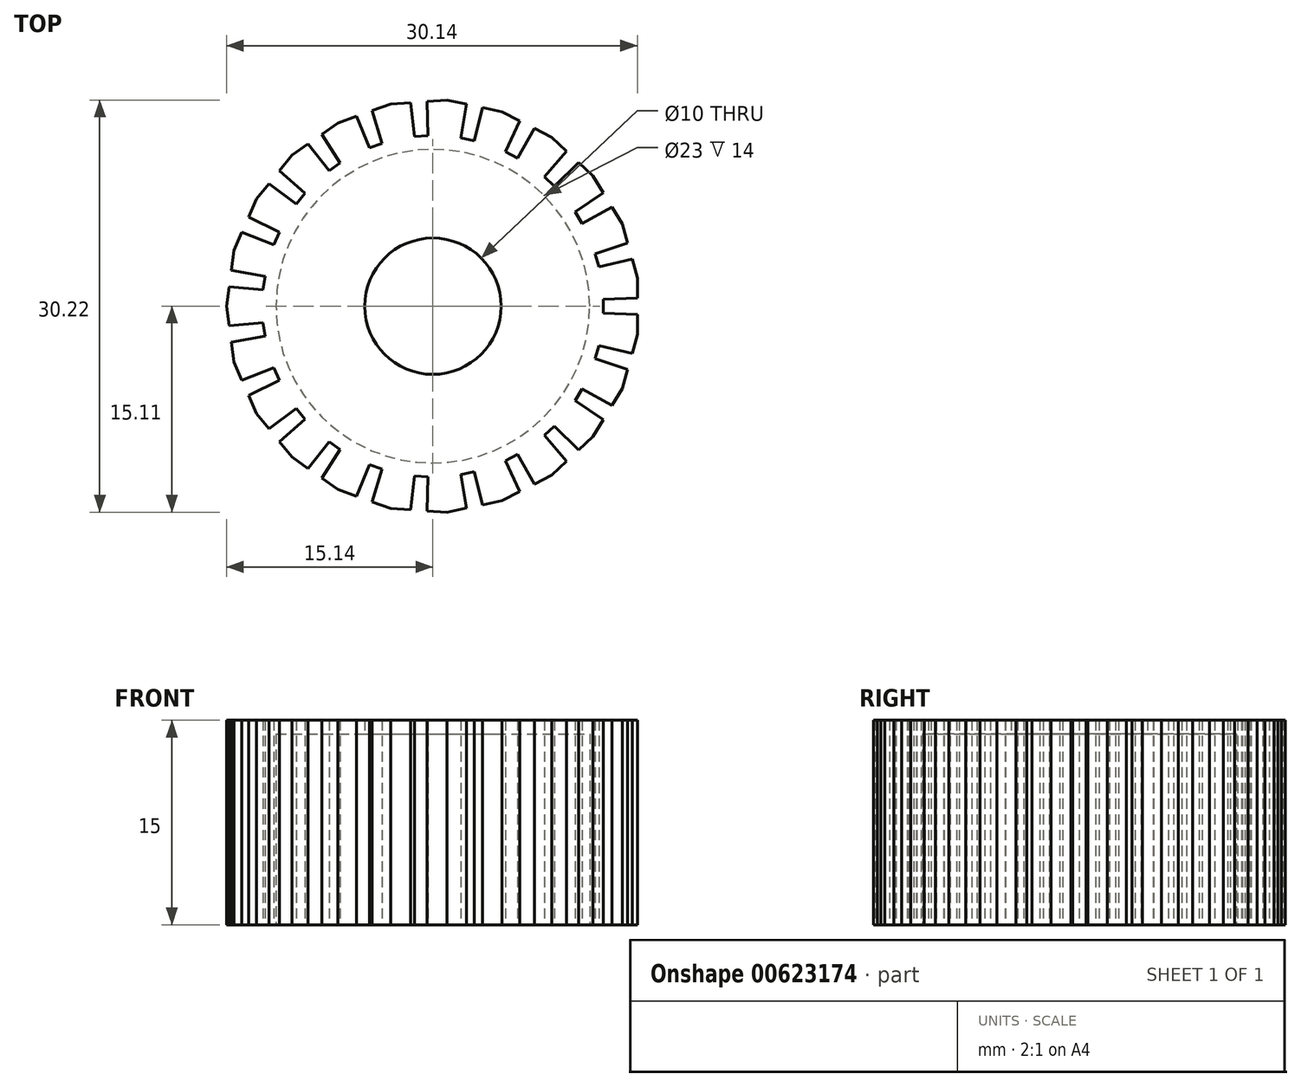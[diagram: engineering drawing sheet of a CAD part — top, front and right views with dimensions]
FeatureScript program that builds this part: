
annotation { "Feature Type Name" : "Feature", "Feature Type Description" : "" }
export const myFeature = defineFeature(function(context is Context, id is Id, definition is map)
    precondition{}
    {
        {
            var Q0;
            Q0=qCreatedBy(makeId("Top.planeOp"),FACE);
            var sketch = newSketch(context, id + "F0", { "sketchPlane" : qUnion([Q0])});
            skCircle(sketch, "E0", {"center": v(0, 0) * mm, "radius": 5 * mm});
            skCircle(sketch, "E1.cCircle", {"center": v(0, 0) * mm, "radius": 15 * mm, "construction": true});
            skLineSegment(sketch, "E1.0", {"start": v(15, 2.06) * mm, "end": v(15, 0.6) * mm});
            skLineSegment(sketch, "E1.1", {"start": v(15, -2.06) * mm, "end": v(13.89, -6.03) * mm, "construction": true});
            skLineSegment(sketch, "E1.2", {"start": v(13.89, -6.03) * mm, "end": v(11.75, -9.56) * mm, "construction": true});
            skLineSegment(sketch, "E1.3", {"start": v(11.75, -9.56) * mm, "end": v(8.73, -12.37) * mm, "construction": true});
            skLineSegment(sketch, "E1.4", {"start": v(8.73, -12.37) * mm, "end": v(5.07, -14.27) * mm, "construction": true});
            skLineSegment(sketch, "E1.5", {"start": v(5.07, -14.27) * mm, "end": v(1.03, -15.1) * mm, "construction": true});
            skLineSegment(sketch, "E1.6", {"start": v(1.03, -15.1) * mm, "end": v(-3.08, -14.82) * mm, "construction": true});
            skLineSegment(sketch, "E1.7", {"start": v(-3.08, -14.82) * mm, "end": v(-6.97, -13.44) * mm, "construction": true});
            skLineSegment(sketch, "E1.8", {"start": v(-6.97, -13.44) * mm, "end": v(-10.33, -11.07) * mm, "construction": true});
            skLineSegment(sketch, "E1.9", {"start": v(-10.33, -11.07) * mm, "end": v(-12.94, -7.87) * mm, "construction": true});
            skLineSegment(sketch, "E1.10", {"start": v(-12.94, -7.87) * mm, "end": v(-14.58, -4.08) * mm, "construction": true});
            skLineSegment(sketch, "E1.11", {"start": v(-14.58, -4.08) * mm, "end": v(-15.14, 0) * mm, "construction": true});
            skLineSegment(sketch, "E1.12", {"start": v(-15.14, 0) * mm, "end": v(-14.58, 4.08) * mm, "construction": true});
            skLineSegment(sketch, "E1.13", {"start": v(-14.58, 4.08) * mm, "end": v(-12.94, 7.87) * mm, "construction": true});
            skLineSegment(sketch, "E1.14", {"start": v(-12.94, 7.87) * mm, "end": v(-10.33, 11.07) * mm, "construction": true});
            skLineSegment(sketch, "E1.15", {"start": v(-10.33, 11.07) * mm, "end": v(-6.97, 13.44) * mm, "construction": true});
            skLineSegment(sketch, "E1.16", {"start": v(-6.97, 13.44) * mm, "end": v(-3.08, 14.82) * mm, "construction": true});
            skLineSegment(sketch, "E1.17", {"start": v(-3.08, 14.82) * mm, "end": v(1.03, 15.1) * mm, "construction": true});
            skLineSegment(sketch, "E1.18", {"start": v(1.03, 15.1) * mm, "end": v(5.07, 14.27) * mm, "construction": true});
            skLineSegment(sketch, "E1.19", {"start": v(5.07, 14.27) * mm, "end": v(8.73, 12.37) * mm, "construction": true});
            skLineSegment(sketch, "E1.20", {"start": v(8.73, 12.37) * mm, "end": v(11.75, 9.56) * mm, "construction": true});
            skLineSegment(sketch, "E1.21", {"start": v(11.75, 9.56) * mm, "end": v(13.89, 6.03) * mm, "construction": true});
            skLineSegment(sketch, "E1.22", {"start": v(13.89, 6.03) * mm, "end": v(15, 2.06) * mm, "construction": true});
            skPoint(sketch, "E1.0.midPoint", {"position": v(15, 0) * mm});
            skLineSegment(sketch, "E2", {"start": v(15, 0.6) * mm, "end": v(12.5, 0.5) * mm});
            skLineSegment(sketch, "E3", {"start": v(12.5, 0.5) * mm, "end": v(12.5, -0.5) * mm});
            skLineSegment(sketch, "E4", {"start": v(12.5, -0.5) * mm, "end": v(15, -0.6) * mm});
            skLineSegment(sketch, "E5.trimOffspring", {"start": v(15, -0.6) * mm, "end": v(15, -2.06) * mm});
            skLineSegment(sketch, "E6.1.0", {"start": v(13.89, 6.03) * mm, "end": v(14.28, 4.63) * mm});
            skLineSegment(sketch, "E6.1.1", {"start": v(14.28, 4.63) * mm, "end": v(11.9, 3.85) * mm});
            skLineSegment(sketch, "E6.1.2", {"start": v(12.17, 2.9) * mm, "end": v(14.6, 3.46) * mm});
            skLineSegment(sketch, "E6.1.3", {"start": v(11.9, 3.85) * mm, "end": v(12.17, 2.9) * mm});
            skLineSegment(sketch, "E6.1.4", {"start": v(14.6, 3.46) * mm, "end": v(15, 2.06) * mm});
            skLineSegment(sketch, "E6.2.0", {"start": v(11.75, 9.56) * mm, "end": v(12.5, 8.31) * mm});
            skLineSegment(sketch, "E6.2.1", {"start": v(12.5, 8.31) * mm, "end": v(10.42, 6.92) * mm});
            skLineSegment(sketch, "E6.2.2", {"start": v(10.94, 6.07) * mm, "end": v(13.13, 7.27) * mm});
            skLineSegment(sketch, "E6.2.3", {"start": v(10.42, 6.92) * mm, "end": v(10.94, 6.07) * mm});
            skLineSegment(sketch, "E6.2.4", {"start": v(13.13, 7.27) * mm, "end": v(13.89, 6.03) * mm});
            skLineSegment(sketch, "E6.3.0", {"start": v(8.73, 12.37) * mm, "end": v(9.8, 11.38) * mm});
            skLineSegment(sketch, "E6.3.1", {"start": v(9.8, 11.38) * mm, "end": v(8.17, 9.48) * mm});
            skLineSegment(sketch, "E6.3.2", {"start": v(8.9, 8.8) * mm, "end": v(10.68, 10.55) * mm});
            skLineSegment(sketch, "E6.3.3", {"start": v(8.17, 9.48) * mm, "end": v(8.9, 8.8) * mm});
            skLineSegment(sketch, "E6.3.4", {"start": v(10.68, 10.55) * mm, "end": v(11.75, 9.56) * mm});
            skLineSegment(sketch, "E6.4.0", {"start": v(5.07, 14.27) * mm, "end": v(6.36, 13.6) * mm});
            skLineSegment(sketch, "E6.4.1", {"start": v(6.36, 13.6) * mm, "end": v(5.3, 11.33) * mm});
            skLineSegment(sketch, "E6.4.2", {"start": v(6.2, 10.87) * mm, "end": v(7.44, 13.04) * mm});
            skLineSegment(sketch, "E6.4.3", {"start": v(5.3, 11.33) * mm, "end": v(6.2, 10.87) * mm});
            skLineSegment(sketch, "E6.4.4", {"start": v(7.44, 13.04) * mm, "end": v(8.73, 12.37) * mm});
            skLineSegment(sketch, "E6.5.0", {"start": v(1.03, 15.1) * mm, "end": v(2.46, 14.81) * mm});
            skLineSegment(sketch, "E6.5.1", {"start": v(2.46, 14.81) * mm, "end": v(2.05, 12.34) * mm});
            skLineSegment(sketch, "E6.5.2", {"start": v(3.03, 12.14) * mm, "end": v(3.65, 14.56) * mm});
            skLineSegment(sketch, "E6.5.3", {"start": v(2.05, 12.34) * mm, "end": v(3.03, 12.14) * mm});
            skLineSegment(sketch, "E6.5.4", {"start": v(3.65, 14.56) * mm, "end": v(5.07, 14.27) * mm});
            skLineSegment(sketch, "E6.6.0", {"start": v(-3.08, 14.82) * mm, "end": v(-1.63, 14.92) * mm});
            skLineSegment(sketch, "E6.6.1", {"start": v(-1.63, 14.92) * mm, "end": v(-1.35, 12.44) * mm});
            skLineSegment(sketch, "E6.6.2", {"start": v(-0.35, 12.5) * mm, "end": v(-0.42, 15) * mm});
            skLineSegment(sketch, "E6.6.3", {"start": v(-1.35, 12.44) * mm, "end": v(-0.35, 12.5) * mm});
            skLineSegment(sketch, "E6.6.4", {"start": v(-0.42, 15) * mm, "end": v(1.03, 15.1) * mm});
            skLineSegment(sketch, "E6.7.0", {"start": v(-6.97, 13.44) * mm, "end": v(-5.6, 13.93) * mm});
            skLineSegment(sketch, "E6.7.1", {"start": v(-5.6, 13.93) * mm, "end": v(-4.66, 11.61) * mm});
            skLineSegment(sketch, "E6.7.2", {"start": v(-3.71, 11.95) * mm, "end": v(-4.45, 14.34) * mm});
            skLineSegment(sketch, "E6.7.3", {"start": v(-4.66, 11.61) * mm, "end": v(-3.71, 11.95) * mm});
            skLineSegment(sketch, "E6.7.4", {"start": v(-4.45, 14.34) * mm, "end": v(-3.08, 14.82) * mm});
            skLineSegment(sketch, "E6.8.0", {"start": v(-10.33, 11.07) * mm, "end": v(-9.15, 11.9) * mm});
            skLineSegment(sketch, "E6.8.1", {"start": v(-9.15, 11.9) * mm, "end": v(-7.62, 9.92) * mm});
            skLineSegment(sketch, "E6.8.2", {"start": v(-6.8, 10.5) * mm, "end": v(-8.15, 12.6) * mm});
            skLineSegment(sketch, "E6.8.3", {"start": v(-7.62, 9.92) * mm, "end": v(-6.8, 10.5) * mm});
            skLineSegment(sketch, "E6.8.4", {"start": v(-8.15, 12.6) * mm, "end": v(-6.97, 13.44) * mm});
            skLineSegment(sketch, "E6.9.0", {"start": v(-12.94, 7.87) * mm, "end": v(-12.02, 9) * mm});
            skLineSegment(sketch, "E6.9.1", {"start": v(-12.02, 9) * mm, "end": v(-10.01, 7.5) * mm});
            skLineSegment(sketch, "E6.9.2", {"start": v(-9.38, 8.28) * mm, "end": v(-11.25, 9.94) * mm});
            skLineSegment(sketch, "E6.9.3", {"start": v(-10.01, 7.5) * mm, "end": v(-9.38, 8.28) * mm});
            skLineSegment(sketch, "E6.9.4", {"start": v(-11.25, 9.94) * mm, "end": v(-10.33, 11.07) * mm});
            skLineSegment(sketch, "E6.10.0", {"start": v(-14.58, 4.08) * mm, "end": v(-14, 5.42) * mm});
            skLineSegment(sketch, "E6.10.1", {"start": v(-14, 5.42) * mm, "end": v(-11.66, 4.52) * mm});
            skLineSegment(sketch, "E6.10.2", {"start": v(-11.27, 5.44) * mm, "end": v(-13.52, 6.53) * mm});
            skLineSegment(sketch, "E6.10.3", {"start": v(-11.66, 4.52) * mm, "end": v(-11.27, 5.44) * mm});
            skLineSegment(sketch, "E6.10.4", {"start": v(-13.52, 6.53) * mm, "end": v(-12.94, 7.87) * mm});
            skLineSegment(sketch, "E6.11.0", {"start": v(-15.14, 0) * mm, "end": v(-14.94, 1.44) * mm});
            skLineSegment(sketch, "E6.11.1", {"start": v(-14.94, 1.44) * mm, "end": v(-12.45, 1.2) * mm});
            skLineSegment(sketch, "E6.11.2", {"start": v(-12.32, 2.2) * mm, "end": v(-14.78, 2.65) * mm});
            skLineSegment(sketch, "E6.11.3", {"start": v(-12.45, 1.2) * mm, "end": v(-12.32, 2.2) * mm});
            skLineSegment(sketch, "E6.11.4", {"start": v(-14.78, 2.65) * mm, "end": v(-14.58, 4.08) * mm});
            skLineSegment(sketch, "E6.12.0", {"start": v(-14.58, -4.08) * mm, "end": v(-14.78, -2.65) * mm});
            skLineSegment(sketch, "E6.12.1", {"start": v(-14.78, -2.65) * mm, "end": v(-12.32, -2.2) * mm});
            skLineSegment(sketch, "E6.12.2", {"start": v(-12.45, -1.2) * mm, "end": v(-14.94, -1.44) * mm});
            skLineSegment(sketch, "E6.12.3", {"start": v(-12.32, -2.2) * mm, "end": v(-12.45, -1.2) * mm});
            skLineSegment(sketch, "E6.12.4", {"start": v(-14.94, -1.44) * mm, "end": v(-15.14, 0) * mm});
            skLineSegment(sketch, "E6.13.0", {"start": v(-12.94, -7.87) * mm, "end": v(-13.52, -6.53) * mm});
            skLineSegment(sketch, "E6.13.1", {"start": v(-13.52, -6.53) * mm, "end": v(-11.27, -5.44) * mm});
            skLineSegment(sketch, "E6.13.2", {"start": v(-11.66, -4.52) * mm, "end": v(-14, -5.42) * mm});
            skLineSegment(sketch, "E6.13.3", {"start": v(-11.27, -5.44) * mm, "end": v(-11.66, -4.52) * mm});
            skLineSegment(sketch, "E6.13.4", {"start": v(-14, -5.42) * mm, "end": v(-14.58, -4.08) * mm});
            skLineSegment(sketch, "E6.14.0", {"start": v(-10.33, -11.07) * mm, "end": v(-11.25, -9.94) * mm});
            skLineSegment(sketch, "E6.14.1", {"start": v(-11.25, -9.94) * mm, "end": v(-9.38, -8.28) * mm});
            skLineSegment(sketch, "E6.14.2", {"start": v(-10.01, -7.5) * mm, "end": v(-12.02, -9) * mm});
            skLineSegment(sketch, "E6.14.3", {"start": v(-9.38, -8.28) * mm, "end": v(-10.01, -7.5) * mm});
            skLineSegment(sketch, "E6.14.4", {"start": v(-12.02, -9) * mm, "end": v(-12.94, -7.87) * mm});
            skLineSegment(sketch, "E6.15.0", {"start": v(-6.97, -13.44) * mm, "end": v(-8.15, -12.6) * mm});
            skLineSegment(sketch, "E6.15.1", {"start": v(-8.15, -12.6) * mm, "end": v(-6.8, -10.5) * mm});
            skLineSegment(sketch, "E6.15.2", {"start": v(-7.62, -9.92) * mm, "end": v(-9.15, -11.9) * mm});
            skLineSegment(sketch, "E6.15.3", {"start": v(-6.8, -10.5) * mm, "end": v(-7.62, -9.92) * mm});
            skLineSegment(sketch, "E6.15.4", {"start": v(-9.15, -11.9) * mm, "end": v(-10.33, -11.07) * mm});
            skLineSegment(sketch, "E6.16.0", {"start": v(-3.08, -14.82) * mm, "end": v(-4.45, -14.34) * mm});
            skLineSegment(sketch, "E6.16.1", {"start": v(-4.45, -14.34) * mm, "end": v(-3.71, -11.95) * mm});
            skLineSegment(sketch, "E6.16.2", {"start": v(-4.66, -11.61) * mm, "end": v(-5.6, -13.93) * mm});
            skLineSegment(sketch, "E6.16.3", {"start": v(-3.71, -11.95) * mm, "end": v(-4.66, -11.61) * mm});
            skLineSegment(sketch, "E6.16.4", {"start": v(-5.6, -13.93) * mm, "end": v(-6.97, -13.44) * mm});
            skLineSegment(sketch, "E6.17.0", {"start": v(1.03, -15.1) * mm, "end": v(-0.42, -15) * mm});
            skLineSegment(sketch, "E6.17.1", {"start": v(-0.42, -15) * mm, "end": v(-0.35, -12.5) * mm});
            skLineSegment(sketch, "E6.17.2", {"start": v(-1.35, -12.44) * mm, "end": v(-1.63, -14.92) * mm});
            skLineSegment(sketch, "E6.17.3", {"start": v(-0.35, -12.5) * mm, "end": v(-1.35, -12.44) * mm});
            skLineSegment(sketch, "E6.17.4", {"start": v(-1.63, -14.92) * mm, "end": v(-3.08, -14.82) * mm});
            skLineSegment(sketch, "E6.18.0", {"start": v(5.07, -14.27) * mm, "end": v(3.65, -14.56) * mm});
            skLineSegment(sketch, "E6.18.1", {"start": v(3.65, -14.56) * mm, "end": v(3.03, -12.14) * mm});
            skLineSegment(sketch, "E6.18.2", {"start": v(2.05, -12.34) * mm, "end": v(2.46, -14.81) * mm});
            skLineSegment(sketch, "E6.18.3", {"start": v(3.03, -12.14) * mm, "end": v(2.05, -12.34) * mm});
            skLineSegment(sketch, "E6.18.4", {"start": v(2.46, -14.81) * mm, "end": v(1.03, -15.1) * mm});
            skLineSegment(sketch, "E6.19.0", {"start": v(8.73, -12.37) * mm, "end": v(7.44, -13.04) * mm});
            skLineSegment(sketch, "E6.19.1", {"start": v(7.44, -13.04) * mm, "end": v(6.2, -10.87) * mm});
            skLineSegment(sketch, "E6.19.2", {"start": v(5.3, -11.33) * mm, "end": v(6.36, -13.6) * mm});
            skLineSegment(sketch, "E6.19.3", {"start": v(6.2, -10.87) * mm, "end": v(5.3, -11.33) * mm});
            skLineSegment(sketch, "E6.19.4", {"start": v(6.36, -13.6) * mm, "end": v(5.07, -14.27) * mm});
            skLineSegment(sketch, "E6.20.0", {"start": v(11.75, -9.56) * mm, "end": v(10.68, -10.55) * mm});
            skLineSegment(sketch, "E6.20.1", {"start": v(10.68, -10.55) * mm, "end": v(8.9, -8.8) * mm});
            skLineSegment(sketch, "E6.20.2", {"start": v(8.17, -9.48) * mm, "end": v(9.8, -11.38) * mm});
            skLineSegment(sketch, "E6.20.3", {"start": v(8.9, -8.8) * mm, "end": v(8.17, -9.48) * mm});
            skLineSegment(sketch, "E6.20.4", {"start": v(9.8, -11.38) * mm, "end": v(8.73, -12.37) * mm});
            skLineSegment(sketch, "E6.21.0", {"start": v(13.89, -6.03) * mm, "end": v(13.13, -7.27) * mm});
            skLineSegment(sketch, "E6.21.1", {"start": v(13.13, -7.27) * mm, "end": v(10.94, -6.07) * mm});
            skLineSegment(sketch, "E6.21.2", {"start": v(10.42, -6.92) * mm, "end": v(12.5, -8.31) * mm});
            skLineSegment(sketch, "E6.21.3", {"start": v(10.94, -6.07) * mm, "end": v(10.42, -6.92) * mm});
            skLineSegment(sketch, "E6.21.4", {"start": v(12.5, -8.31) * mm, "end": v(11.75, -9.56) * mm});
            skLineSegment(sketch, "E6.22.0", {"start": v(15, -2.06) * mm, "end": v(14.6, -3.46) * mm});
            skLineSegment(sketch, "E6.22.1", {"start": v(14.6, -3.46) * mm, "end": v(12.17, -2.9) * mm});
            skLineSegment(sketch, "E6.22.2", {"start": v(11.9, -3.85) * mm, "end": v(14.28, -4.63) * mm});
            skLineSegment(sketch, "E6.22.3", {"start": v(12.17, -2.9) * mm, "end": v(11.9, -3.85) * mm});
            skLineSegment(sketch, "E6.22.4", {"start": v(14.28, -4.63) * mm, "end": v(13.89, -6.03) * mm});
            skSolve(sketch);
        }
        {
            var Q0;
            Q0=qSketchRegion(id+"F0",true);
            extrude(context, id + "F1", {"entities" : qUnion([Q0]), "depth" : 15 * mm, "offsetDistance" : 25 * mm});
        }
        {
            var Q0;
            Q0=makeQuery(id+"F1.opExtrude","CAP_FACE",FACE,{"disambiguationData":[OSD([sQuery(id+"F0.wireOp",EDGE,"E0"),sQuery(id+"F0.wireOp",EDGE,"E1.0"),sQuery(id+"F0.wireOp",EDGE,"E2"),sQuery(id+"F0.wireOp",EDGE,"E3"),sQuery(id+"F0.wireOp",EDGE,"E4"),sQuery(id+"F0.wireOp",EDGE,"E5.trimOffspring"),sQuery(id+"F0.wireOp",EDGE,"E6.1.0"),sQuery(id+"F0.wireOp",EDGE,"E6.1.1"),sQuery(id+"F0.wireOp",EDGE,"E6.1.2"),sQuery(id+"F0.wireOp",EDGE,"E6.1.3"),sQuery(id+"F0.wireOp",EDGE,"E6.1.4"),sQuery(id+"F0.wireOp",EDGE,"E6.2.0"),sQuery(id+"F0.wireOp",EDGE,"E6.2.1"),sQuery(id+"F0.wireOp",EDGE,"E6.2.2"),sQuery(id+"F0.wireOp",EDGE,"E6.2.3"),sQuery(id+"F0.wireOp",EDGE,"E6.2.4"),sQuery(id+"F0.wireOp",EDGE,"E6.3.0"),sQuery(id+"F0.wireOp",EDGE,"E6.3.1"),sQuery(id+"F0.wireOp",EDGE,"E6.3.2"),sQuery(id+"F0.wireOp",EDGE,"E6.3.3"),sQuery(id+"F0.wireOp",EDGE,"E6.3.4"),sQuery(id+"F0.wireOp",EDGE,"E6.4.0"),sQuery(id+"F0.wireOp",EDGE,"E6.4.1"),sQuery(id+"F0.wireOp",EDGE,"E6.4.2"),sQuery(id+"F0.wireOp",EDGE,"E6.4.3"),sQuery(id+"F0.wireOp",EDGE,"E6.4.4"),sQuery(id+"F0.wireOp",EDGE,"E6.5.0"),sQuery(id+"F0.wireOp",EDGE,"E6.5.1"),sQuery(id+"F0.wireOp",EDGE,"E6.5.2"),sQuery(id+"F0.wireOp",EDGE,"E6.5.3"),sQuery(id+"F0.wireOp",EDGE,"E6.5.4"),sQuery(id+"F0.wireOp",EDGE,"E6.6.0"),sQuery(id+"F0.wireOp",EDGE,"E6.6.1"),sQuery(id+"F0.wireOp",EDGE,"E6.6.2"),sQuery(id+"F0.wireOp",EDGE,"E6.6.3"),sQuery(id+"F0.wireOp",EDGE,"E6.6.4"),sQuery(id+"F0.wireOp",EDGE,"E6.7.0"),sQuery(id+"F0.wireOp",EDGE,"E6.7.1"),sQuery(id+"F0.wireOp",EDGE,"E6.7.2"),sQuery(id+"F0.wireOp",EDGE,"E6.7.3"),sQuery(id+"F0.wireOp",EDGE,"E6.7.4"),sQuery(id+"F0.wireOp",EDGE,"E6.8.0"),sQuery(id+"F0.wireOp",EDGE,"E6.8.1"),sQuery(id+"F0.wireOp",EDGE,"E6.8.2"),sQuery(id+"F0.wireOp",EDGE,"E6.8.3"),sQuery(id+"F0.wireOp",EDGE,"E6.8.4"),sQuery(id+"F0.wireOp",EDGE,"E6.9.0"),sQuery(id+"F0.wireOp",EDGE,"E6.9.1"),sQuery(id+"F0.wireOp",EDGE,"E6.9.2"),sQuery(id+"F0.wireOp",EDGE,"E6.9.3"),sQuery(id+"F0.wireOp",EDGE,"E6.9.4"),sQuery(id+"F0.wireOp",EDGE,"E6.10.0"),sQuery(id+"F0.wireOp",EDGE,"E6.10.1"),sQuery(id+"F0.wireOp",EDGE,"E6.10.2"),sQuery(id+"F0.wireOp",EDGE,"E6.10.3"),sQuery(id+"F0.wireOp",EDGE,"E6.10.4"),sQuery(id+"F0.wireOp",EDGE,"E6.11.0"),sQuery(id+"F0.wireOp",EDGE,"E6.11.1"),sQuery(id+"F0.wireOp",EDGE,"E6.11.2"),sQuery(id+"F0.wireOp",EDGE,"E6.11.3"),sQuery(id+"F0.wireOp",EDGE,"E6.11.4"),sQuery(id+"F0.wireOp",EDGE,"E6.12.0"),sQuery(id+"F0.wireOp",EDGE,"E6.12.1"),sQuery(id+"F0.wireOp",EDGE,"E6.12.2"),sQuery(id+"F0.wireOp",EDGE,"E6.12.3"),sQuery(id+"F0.wireOp",EDGE,"E6.12.4"),sQuery(id+"F0.wireOp",EDGE,"E6.13.0"),sQuery(id+"F0.wireOp",EDGE,"E6.13.1"),sQuery(id+"F0.wireOp",EDGE,"E6.13.2"),sQuery(id+"F0.wireOp",EDGE,"E6.13.3"),sQuery(id+"F0.wireOp",EDGE,"E6.13.4"),sQuery(id+"F0.wireOp",EDGE,"E6.14.0"),sQuery(id+"F0.wireOp",EDGE,"E6.14.1"),sQuery(id+"F0.wireOp",EDGE,"E6.14.2"),sQuery(id+"F0.wireOp",EDGE,"E6.14.3"),sQuery(id+"F0.wireOp",EDGE,"E6.14.4"),sQuery(id+"F0.wireOp",EDGE,"E6.15.0"),sQuery(id+"F0.wireOp",EDGE,"E6.15.1"),sQuery(id+"F0.wireOp",EDGE,"E6.15.2"),sQuery(id+"F0.wireOp",EDGE,"E6.15.3"),sQuery(id+"F0.wireOp",EDGE,"E6.15.4"),sQuery(id+"F0.wireOp",EDGE,"E6.16.0"),sQuery(id+"F0.wireOp",EDGE,"E6.16.1"),sQuery(id+"F0.wireOp",EDGE,"E6.16.2"),sQuery(id+"F0.wireOp",EDGE,"E6.16.3"),sQuery(id+"F0.wireOp",EDGE,"E6.16.4"),sQuery(id+"F0.wireOp",EDGE,"E6.17.0"),sQuery(id+"F0.wireOp",EDGE,"E6.17.1"),sQuery(id+"F0.wireOp",EDGE,"E6.17.2"),sQuery(id+"F0.wireOp",EDGE,"E6.17.3"),sQuery(id+"F0.wireOp",EDGE,"E6.17.4"),sQuery(id+"F0.wireOp",EDGE,"E6.18.0"),sQuery(id+"F0.wireOp",EDGE,"E6.18.1"),sQuery(id+"F0.wireOp",EDGE,"E6.18.2"),sQuery(id+"F0.wireOp",EDGE,"E6.18.3"),sQuery(id+"F0.wireOp",EDGE,"E6.18.4"),sQuery(id+"F0.wireOp",EDGE,"E6.19.0"),sQuery(id+"F0.wireOp",EDGE,"E6.19.1"),sQuery(id+"F0.wireOp",EDGE,"E6.19.2"),sQuery(id+"F0.wireOp",EDGE,"E6.19.3"),sQuery(id+"F0.wireOp",EDGE,"E6.19.4"),sQuery(id+"F0.wireOp",EDGE,"E6.20.0"),sQuery(id+"F0.wireOp",EDGE,"E6.20.1"),sQuery(id+"F0.wireOp",EDGE,"E6.20.2"),sQuery(id+"F0.wireOp",EDGE,"E6.20.3"),sQuery(id+"F0.wireOp",EDGE,"E6.20.4"),sQuery(id+"F0.wireOp",EDGE,"E6.21.0"),sQuery(id+"F0.wireOp",EDGE,"E6.21.1"),sQuery(id+"F0.wireOp",EDGE,"E6.21.2"),sQuery(id+"F0.wireOp",EDGE,"E6.21.3"),sQuery(id+"F0.wireOp",EDGE,"E6.21.4"),sQuery(id+"F0.wireOp",EDGE,"E6.22.0"),sQuery(id+"F0.wireOp",EDGE,"E6.22.1"),sQuery(id+"F0.wireOp",EDGE,"E6.22.2"),sQuery(id+"F0.wireOp",EDGE,"E6.22.3"),sQuery(id+"F0.wireOp",EDGE,"E6.22.4")])],"isStart":true});
            var sketch = newSketch(context, id + "F2", { "sketchPlane" : qUnion([Q0])});
            skCircle(sketch, "E7", {"center": v(0, 0) * mm, "radius": 11.5 * mm});
            skSolve(sketch);
        }
        {
            var Q0;
            Q0=qSketchRegion(id+"F2",true);
            extrude(context, id + "F3", {"entities" : qUnion([Q0]), "operationType" : NewBodyOperationType.REMOVE, "oppositeDirection" : true, "depth" : 14 * mm, "offsetDistance" : 25 * mm});
        }
    });
